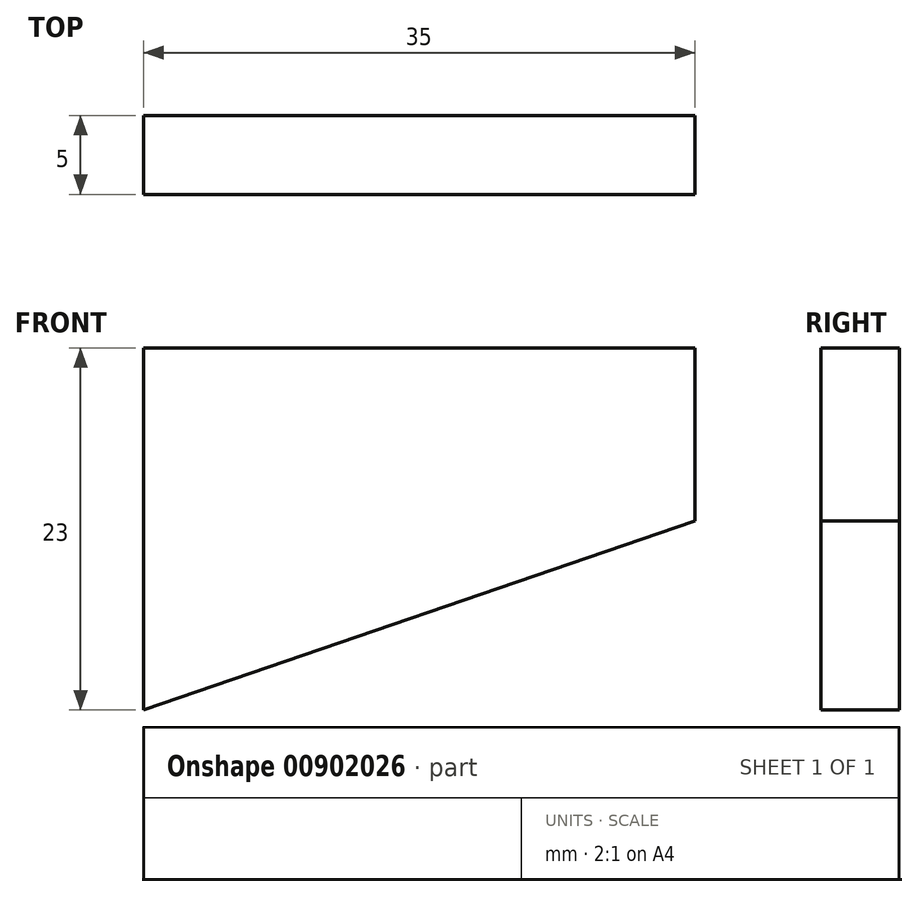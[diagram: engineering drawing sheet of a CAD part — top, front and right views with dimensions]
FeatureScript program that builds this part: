
annotation { "Feature Type Name" : "Feature", "Feature Type Description" : "" }
export const myFeature = defineFeature(function(context is Context, id is Id, definition is map)
    precondition{}
    {
        {
            var Q0;
            Q0=qCreatedBy(makeId("Front.planeOp"),FACE);
            var sketch = newSketch(context, id + "F0", { "sketchPlane" : qUnion([Q0])});
            skLineSegment(sketch, "E0", {"start": v(0, 23) * mm, "end": v(0, 0) * mm});
            skLineSegment(sketch, "E1", {"start": v(0, 0) * mm, "end": v(35, 12) * mm});
            skLineSegment(sketch, "E2", {"start": v(35, 12) * mm, "end": v(35, 23) * mm});
            skLineSegment(sketch, "E3", {"start": v(35, 23) * mm, "end": v(0, 23) * mm});
            skSolve(sketch);
        }
        {
            var Q0;
            Q0 = qSketchRegion(id + "F0", true);
            extrude(context, id + "F1", {"entities" : qUnion([Q0]), "depth" : 5 * mm, "offsetDistance" : 25 * mm});
        }
    });
